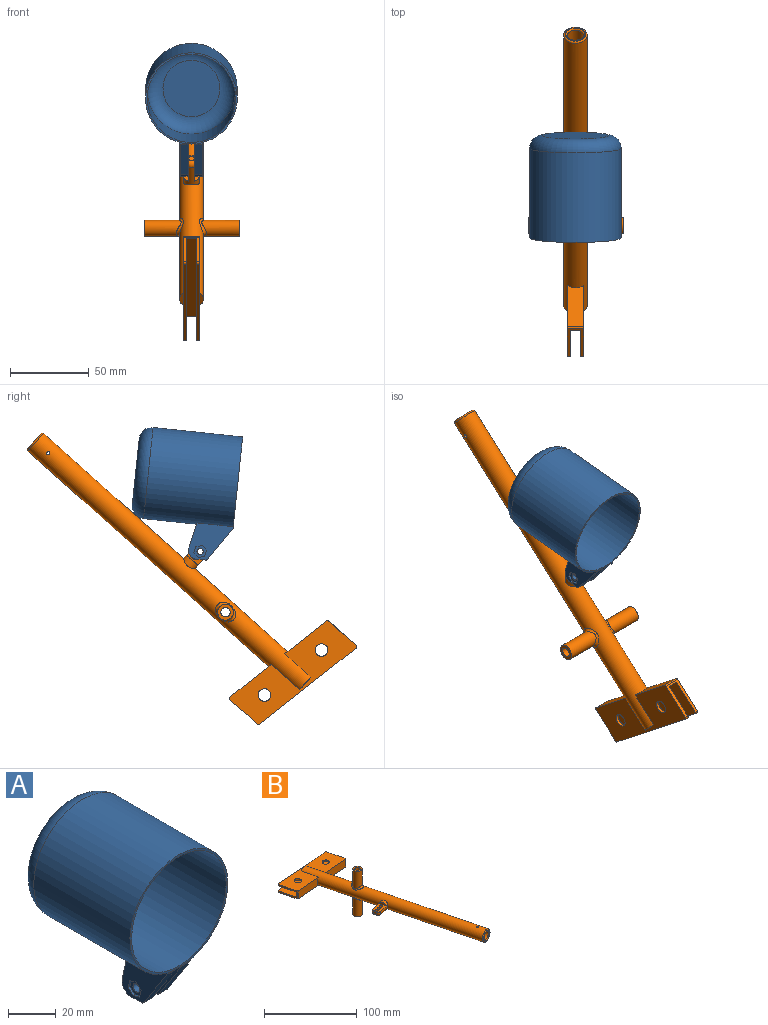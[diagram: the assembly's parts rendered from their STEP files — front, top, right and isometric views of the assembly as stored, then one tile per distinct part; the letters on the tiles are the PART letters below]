
ASSEMBLY  parts=2 mates=1
PART A: 43 faces, bbox 62.8x65x82.4 mm
  f0: plane 6.12x5mm, normal (0,0,-1), area 30.6mm2, adj f4,f5,f14,f15
  f1: cylinder r=2mm len=4mm, axis (-1,0,0), area 50.3mm2, adj f13,f14
  f2: plane 14.78x5mm, normal (0,0.98,0.21), area 75.7mm2, adj f5,f6,f14,f41
  f3: plane 21.08x13.6mm, normal (0,-0.84,-0.54), area 125.4mm2, adj f5,f14,f15,f42
  f4: cylinder r=5mm len=5mm, axis (1,0,0), area 39.3mm2, adj f0,f5,f6,f14
  f5: plane 26.4x22.86mm, normal (-1,0,0), area 372.6mm2, adj f0,f2,f3,f4,f6,f7,f8,f9
  f6: plane 5x2.22mm, normal (0,1,0), area 11.1mm2, adj f2,f4,f5,f14
  f7: plane 2.98x2.74mm, normal (0,0.68,-0.74), area 4mm2, adj f5,f8,f12,f13
  f8: plane 3.86x1.21mm, normal (0,-0.3,-0.95), area 4mm2, adj f5,f7,f9,f13
  f9: plane 3.94x1mm, normal (0,-0.98,-0.22), area 4mm2, adj f5,f8,f10,f13
  f10: plane 2.98x2.74mm, normal (0,-0.68,0.74), area 4mm2, adj f5,f9,f11,f13
  f11: plane 3.86x1.21mm, normal (0,0.3,0.95), area 4mm2, adj f5,f10,f12,f13
  f12: plane 3.94x1mm, normal (0,0.98,0.22), area 4mm2, adj f5,f7,f11,f13
  f13: plane 7.89x7.71mm, normal (-1,0,0), area 29.9mm2, adj f1,f7,f8,f9,f10,f11,f12
  f14: plane 26.4x22.07mm, normal (1,0,0), area 384.3mm2, adj f0,f1,f2,f3,f4,f6,f15,f32
  f15: cylinder r=2mm len=5mm, axis (1,0,0), area 10mm2, adj f0,f3,f5,f14
  f16: plane 3.02x2.69mm, normal (0,0.75,-0.66), area 4mm2, adj f17,f21,f23,f24
  f17: plane 3.84x1.27mm, normal (0,0.95,0.32), area 4mm2, adj f16,f18,f21,f24
  f18: plane 3.96x1mm, normal (0,0.2,0.98), area 4mm2, adj f17,f19,f21,f24
  f19: plane 3.02x2.69mm, normal (0,-0.75,0.66), area 4mm2, adj f18,f20,f21,f24
  f20: plane 3.84x1.27mm, normal (0,-0.95,-0.32), area 4mm2, adj f19,f21,f23,f24
  f21: plane 7.92x7.67mm, normal (1,0,0), area 29.9mm2, adj f16,f17,f18,f19,f20,f22,f23
  f22: cylinder r=2mm len=4mm, axis (-1,0,0), area 50.3mm2, adj f21,f30
  f23: plane 3.96x1mm, normal (0,-0.2,-0.98), area 4mm2, adj f16,f20,f21,f24
  f24: plane 26.4x22.86mm, normal (1,0,0), area 372.6mm2, adj f16,f17,f18,f19,f20,f23,f25,f26
  f25: cylinder r=5mm len=5mm, axis (1,0,0), area 39.3mm2, adj f24,f28,f29,f30
  f26: plane 21.08x13.6mm, normal (0,-0.84,-0.54), area 125.4mm2, adj f24,f30,f31,f40
  f27: plane 14.78x5mm, normal (0,0.98,0.21), area 75.7mm2, adj f24,f28,f30,f39
  f28: plane 5x2.22mm, normal (0,1,0), area 11.1mm2, adj f24,f25,f27,f30
  f29: plane 6.12x5mm, normal (0,0,-1), area 30.6mm2, adj f24,f25,f30,f31
  f30: plane 26.4x22.07mm, normal (-1,0,0), area 384.3mm2, adj f22,f25,f26,f27,f28,f29,f31,f32
  f31: cylinder r=2mm len=5mm, axis (1,0,0), area 10mm2, adj f24,f26,f29,f30
  f32: cylinder r=29mm len=58mm, axis (0,1,0), area 10151.3mm2, adj f5,f14,f24,f30,f33,f37,f39,f40
  f33: plane 58x58mm, normal (0,-1,0), area 179.1mm2, adj f32,f35
  f34: plane 42x42mm, normal (0,1,0), area 1385.4mm2, adj f37
  f35: cylinder r=28mm len=56mm, axis (0,-1,0), area 8796.5mm2, adj f33,f38
  f36: plane 36x36mm, normal (0,-1,0), area 1017.9mm2, adj f38
  f37: torus R=21mm, axis (0,-1,0), area 2060.2mm2, adj f32,f34
  f38: torus R=18mm, axis (0,-1,0), area 2404.8mm2, adj f35,f36
  f39: plane 5x0.86mm, normal (0,1,0), area 1.9mm2, adj f24,f27,f30,f32
  f40: plane 5x0.86mm, normal (0,-1,0), area 1.9mm2, adj f24,f26,f30,f32
  f41: plane 5x0.86mm, normal (0,1,0), area 1.9mm2, adj f2,f5,f14,f32
  f42: plane 5x0.86mm, normal (0,-1,0), area 1.9mm2, adj f3,f5,f14,f32
PART B: 50 faces, bbox 104.8x230.6x60.5 mm
  f0: plane 34.14x11.26mm, normal (0.07,-1,0), area 335.7mm2, adj f1,f2,f16,f22
  f1: plane 85.48x30.33mm, normal (0,0,1), area 1651.8mm2, adj f0,f3,f4,f9,f10,f13,f14,f15
  f2: plane 85.48x30.33mm, normal (0,0,-1), area 1651.8mm2, adj f0,f4,f5,f9,f10,f11,f12,f15
  f3: plane 77.76x5.68mm, normal (-0.07,1,0), area 155.9mm2, adj f1,f6,f17,f20
  f4: plane 34.29x11.26mm, normal (0.07,-1,0), area 337.3mm2, adj f1,f2,f15,f22
  f5: plane 77.76x5.68mm, normal (-0.07,1,0), area 155.9mm2, adj f2,f7,f18,f19
  f6: plane 85.25x28.42mm, normal (0,0,-1), area 1739mm2, adj f3,f8,f9,f10,f13,f14,f17,f20
  f7: plane 85.25x28.42mm, normal (0,0,1), area 1739mm2, adj f5,f8,f9,f10,f11,f12,f18,f19
  f8: plane 79.79x6.5mm, normal (-0.07,1,0), area 520mm2, adj f6,f7,f9,f10
  f9: plane 22.64x10.5mm, normal (-0.97,-0.24,0), area 101.2mm2, adj f1,f2,f6,f7,f8,f15,f19,f20
  f10: plane 22.64x10.5mm, normal (0.97,0.24,0), area 98.9mm2, adj f1,f2,f6,f7,f8,f16,f17,f18
  f11: cylinder r=4mm len=8mm, axis (0,0,-1), area 50.3mm2, adj f2,f7
  f12: cylinder r=4mm len=8mm, axis (0,0,-1), area 50.3mm2, adj f2,f7
  f13: cylinder r=4mm len=8mm, axis (0,0,-1), area 50.3mm2, adj f1,f6
  f14: cylinder r=4mm len=8mm, axis (0,0,-1), area 50.3mm2, adj f1,f6
  f15: cylinder r=1mm len=10.5mm, axis (0,0,-1), area 14.7mm2, adj f1,f2,f4,f9
  f16: cylinder r=1mm len=10.5mm, axis (0,0,1), area 18.3mm2, adj f0,f1,f2,f10
  f17: cylinder r=1mm len=2mm, axis (0,0,1), area 2.8mm2, adj f1,f3,f6,f10
  f18: cylinder r=1mm len=2mm, axis (0,0,1), area 2.8mm2, adj f2,f5,f7,f10
  f19: cylinder r=1mm len=2mm, axis (0,0,1), area 3.5mm2, adj f2,f5,f7,f9
  f20: cylinder r=1mm len=2mm, axis (0,0,1), area 3.5mm2, adj f1,f3,f6,f9
  f21: plane 10.39x2.62mm, normal (-0.24,0.97,0), area 16.6mm2, adj f2,f22
  f22: cylinder r=7.5mm len=225.7mm, axis (-0.24,0.97,0), area 9901.1mm2, adj f0,f1,f2,f4,f21,f23,f34,f44
  f23: plane 10.39x2.62mm, normal (-0.24,0.97,0), area 16.6mm2, adj f1,f22
  f24: plane 13x12.6mm, normal (0.24,-0.97,0), area 19.6mm2, adj f46,f47
  f25: plane 10x10mm, normal (0,0,1), area 50.3mm2, adj f26,f43
  f26: cylinder r=5mm len=23.19mm, axis (0,0,1), area 674.3mm2, adj f25,f49
  f27: cylinder r=5mm len=23.94mm, axis (0,0,1), area 697.9mm2, adj f28,f48
  f28: plane 10x10mm, normal (0,0,-1), area 50.3mm2, adj f27,f42
  f29: plane 8.89x3mm, normal (-0.97,-0.24,0), area 19.8mm2, adj f30,f34
  f30: plane 16.05x11.91mm, normal (0,0,-1), area 95.4mm2, adj f29,f34,f35,f36,f37,f38,f39
  f31: plane 4x3.88mm, normal (-0.97,-0.24,0), area 12.6mm2, adj f38,f39
  f32: plane 16.05x11.91mm, normal (0,0,1), area 95.4mm2, adj f33,f34,f35,f36,f37,f38,f39
  f33: plane 8.89x3mm, normal (-0.97,-0.24,0), area 19.8mm2, adj f32,f34
  f34: cylinder r=5mm len=18.71mm, axis (0.97,0.24,0), area 217.4mm2, adj f22,f29,f30,f32,f33,f38,f39
  f35: cylinder r=2mm len=4mm, axis (0,0,-1), area 50.3mm2, adj f30,f32
  f36: cylinder r=2mm len=4mm, axis (0,0,-1), area 50.3mm2, adj f30,f32
  f37: cylinder r=2mm len=4mm, axis (0,0,-1), area 50.3mm2, adj f30,f32
  f38: torus R=2mm, axis (-0.97,-0.24,0), area 20.3mm2, adj f30,f31,f32,f34
  f39: torus R=2mm, axis (-0.97,-0.24,0), area 20.3mm2, adj f30,f31,f32,f34
  f40: cylinder r=5mm len=195.39mm, axis (0.24,-0.97,0), area 6185.9mm2, adj f41,f42,f43,f44,f45,f46
  f41: plane 10x9.7mm, normal (0.24,-0.97,0), area 78.5mm2, adj f40
  f42: cylinder r=3mm len=26.33mm, axis (0,0,-1), area 485.2mm2, adj f28,f40
  f43: cylinder r=3mm len=25.58mm, axis (0,0,-1), area 471mm2, adj f25,f40
  f44: cylinder r=1mm len=2.53mm, axis (0,0,1), area 15.9mm2, adj f22,f40
  f45: cylinder r=1mm len=2.53mm, axis (0,0,1), area 15.9mm2, adj f22,f40
  f46: torus R=6mm, axis (0.24,-0.97,0), area 52.9mm2, adj f24,f40
  f47: torus R=6.5mm, axis (0.24,-0.97,0), area 70.4mm2, adj f22,f24
  f48: bspline ~13.86x11.26mm, area 83mm2, adj f22,f27
  f49: bspline ~13.85x11.26mm, area 83mm2, adj f22,f26
PLACE A rot(axis=(1,0,0),6deg) t=(10.93,2.14,-5.16)mm
PLACE B rot(axis=(-0.66,-0.35,0.66),141.2deg) t=(16.18,-49.25,-99.48)mm fixed
MATE revolute A.f1 <-> B.f35  axis (1,0,0) through (8.93,-4.47,-11.81)mm
